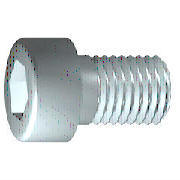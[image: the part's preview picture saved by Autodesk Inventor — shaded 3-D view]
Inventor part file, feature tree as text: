
AUTODESK INVENTOR PART (.ipt)
format: ipt  version: 2018 (Build 220112000, 112)  size: 182,272 bytes
history: native  units: mm (DEFAULTED — no unit token found)
features: sketch x2, extrude x1, plane x1, fillet x1
ambient origin geometry x7: Origin, YZ Plane, XY Plane, X Axis, Y Axis, Z Axis, Center Point
bodies: Solid1 (feature_tree), Body (feature_tree)
feature tree (5):
  extrude  "Slot"  Depth=5.0mm
  plane  "Work Plane1"
  fillet  "Fillet2"  Radius=5.0mm
  sketch  "Sketch1"  dims[d1=22.0mm d2=0.49086mm d3=5.0mm]
  sketch  "Sketch2"  dims[d4=2.5mm d5=60.0deg d6=5.0mm d7=5.0mm d8=4.618802mm d9=8.5mm d10=90.0deg d11=10.0mm d12=0.0mm d13=22.0mm d14=0.0mm d15=0.49076mm d16=0.49076mm d17=0.5mm d19=0.0mm d26=55.0mm d27=45.0deg d28=0.0mm d29=0.0mm d30=0.1mm]
